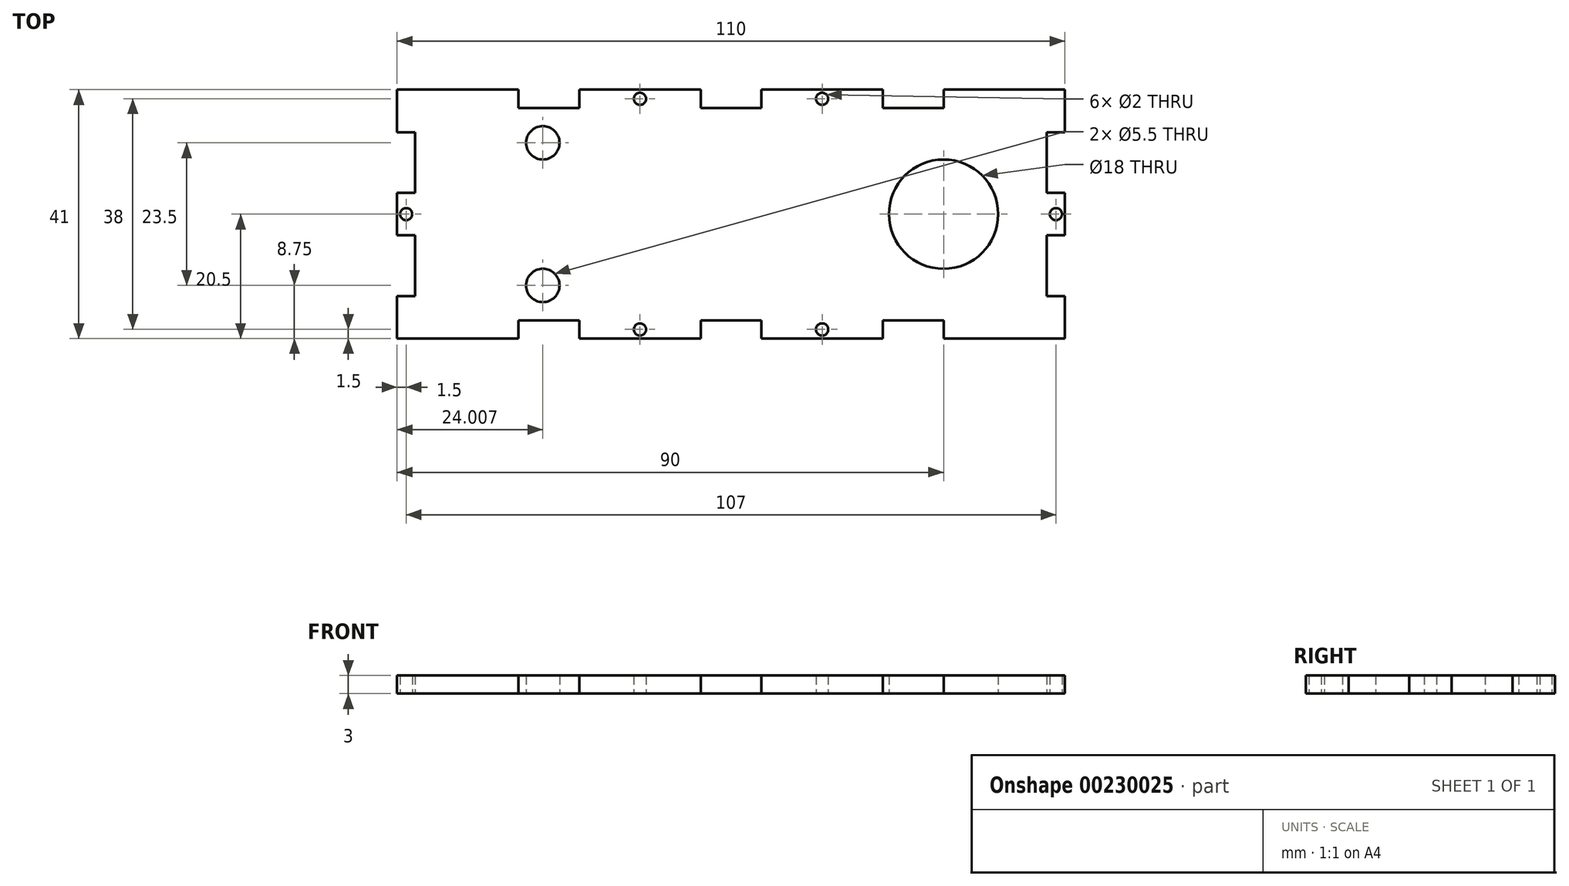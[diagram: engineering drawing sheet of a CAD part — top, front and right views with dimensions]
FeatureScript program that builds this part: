
annotation { "Feature Type Name" : "Feature", "Feature Type Description" : "" }
export const myFeature = defineFeature(function(context is Context, id is Id, definition is map)
    precondition{}
    {
        {
            var Q0;
            Q0=qCreatedBy(makeId("Top.planeOp"),FACE);
            var sketch = newSketch(context, id + "F0", { "sketchPlane" : qUnion([Q0])});
            skLineSegment(sketch, "E0", {"start": v(0, 0) * mm, "end": v(0, 7) * mm});
            skLineSegment(sketch, "E1", {"start": v(0, 7) * mm, "end": v(3, 7) * mm});
            skLineSegment(sketch, "E2", {"start": v(3, 7) * mm, "end": v(3, 17) * mm});
            skLineSegment(sketch, "E3", {"start": v(3, 17) * mm, "end": v(0, 17) * mm});
            skLineSegment(sketch, "E4", {"start": v(0, 17) * mm, "end": v(0, 24) * mm});
            skLineSegment(sketch, "E5", {"start": v(0, 24) * mm, "end": v(3, 24) * mm});
            skLineSegment(sketch, "E6", {"start": v(3, 24) * mm, "end": v(3, 34) * mm});
            skLineSegment(sketch, "E7", {"start": v(3, 34) * mm, "end": v(0, 34) * mm});
            skLineSegment(sketch, "E8", {"start": v(0, 34) * mm, "end": v(0, 41) * mm});
            skLineSegment(sketch, "E9", {"start": v(0, 41) * mm, "end": v(20, 41) * mm});
            skLineSegment(sketch, "E10", {"start": v(20, 41) * mm, "end": v(20, 38) * mm});
            skLineSegment(sketch, "E11", {"start": v(20, 38) * mm, "end": v(30, 38) * mm});
            skLineSegment(sketch, "E12", {"start": v(30, 38) * mm, "end": v(30, 41) * mm});
            skLineSegment(sketch, "E13", {"start": v(30, 41) * mm, "end": v(50, 41) * mm});
            skLineSegment(sketch, "E14", {"start": v(50, 38) * mm, "end": v(55, 38) * mm});
            skLineSegment(sketch, "E15", {"start": v(50, 41) * mm, "end": v(50, 38) * mm});
            skLineSegment(sketch, "E16", {"start": v(55, 40.92) * mm, "end": v(55, 0) * mm, "construction": true});
            skLineSegment(sketch, "E17", {"start": v(0, 20.5) * mm, "end": v(55, 20.5) * mm, "construction": true});
            skCircle(sketch, "E18", {"center": v(40, 39.5) * mm, "radius": 1 * mm});
            skPoint(sketch, "E18.centerSnap0", {"position": v(40, 41) * mm});
            skPoint(sketch, "E18.centerSnap1", {"position": v(50, 39.5) * mm});
            skCircle(sketch, "E19", {"center": v(1.5, 20.5) * mm, "radius": 1 * mm});
            skPoint(sketch, "E19.centerSnap0", {"position": v(1.5, 24) * mm});
            skLineSegment(sketch, "E20.MirrorCS", {"start": v(20, 0) * mm, "end": v(20, 3) * mm});
            skLineSegment(sketch, "E21.MirrorCS", {"start": v(50, 0) * mm, "end": v(50, 3) * mm});
            skLineSegment(sketch, "E22.MirrorCS", {"start": v(30, 3) * mm, "end": v(30, 0) * mm});
            skCircle(sketch, "E23.MirrorC", {"center": v(40, 1.5) * mm, "radius": 1 * mm});
            skLineSegment(sketch, "E24.MirrorCS", {"start": v(20, 3) * mm, "end": v(30, 3) * mm});
            skLineSegment(sketch, "E25.MirrorCS", {"start": v(30, 0) * mm, "end": v(50, 0) * mm});
            skPoint(sketch, "E26.MirrorP", {"position": v(40, 0) * mm});
            skPoint(sketch, "E27.MirrorP", {"position": v(50, 1.5) * mm});
            skLineSegment(sketch, "E28.MirrorCS", {"start": v(0, 0) * mm, "end": v(20, 0) * mm});
            skLineSegment(sketch, "E29.MirrorCS", {"start": v(50, 3) * mm, "end": v(55, 3) * mm});
            skLineSegment(sketch, "E30.MirrorCS", {"start": v(60, 41) * mm, "end": v(60, 38) * mm});
            skLineSegment(sketch, "E31.MirrorCS", {"start": v(107, 34) * mm, "end": v(110, 34) * mm});
            skLineSegment(sketch, "E32.MirrorCS", {"start": v(110, 24) * mm, "end": v(107, 24) * mm});
            skLineSegment(sketch, "E33.MirrorCS", {"start": v(110, 7) * mm, "end": v(107, 7) * mm});
            skLineSegment(sketch, "E34.MirrorCS", {"start": v(107, 17) * mm, "end": v(110, 17) * mm});
            skLineSegment(sketch, "E35.MirrorCS", {"start": v(90, 41) * mm, "end": v(90, 38) * mm});
            skLineSegment(sketch, "E36.MirrorCS", {"start": v(80, 38) * mm, "end": v(80, 41) * mm});
            skLineSegment(sketch, "E37.MirrorCS", {"start": v(60, 0) * mm, "end": v(60, 3) * mm});
            skCircle(sketch, "E38.MirrorC", {"center": v(108.5, 20.5) * mm, "radius": 1 * mm});
            skCircle(sketch, "E39.MirrorC", {"center": v(70, 1.5) * mm, "radius": 1 * mm});
            skCircle(sketch, "E40.MirrorC", {"center": v(70, 39.5) * mm, "radius": 1 * mm});
            skLineSegment(sketch, "E41.MirrorCS", {"start": v(110, 17) * mm, "end": v(110, 24) * mm});
            skLineSegment(sketch, "E42.MirrorCS", {"start": v(80, 41) * mm, "end": v(60, 41) * mm});
            skPoint(sketch, "E43.MirrorP", {"position": v(108.5, 24) * mm});
            skLineSegment(sketch, "E44.MirrorCS", {"start": v(90, 3) * mm, "end": v(80, 3) * mm});
            skLineSegment(sketch, "E45.MirrorCS", {"start": v(110, 0) * mm, "end": v(90, 0) * mm});
            skPoint(sketch, "E46.MirrorP", {"position": v(70, 41) * mm});
            skLineSegment(sketch, "E47.MirrorCS", {"start": v(107, 24) * mm, "end": v(107, 34) * mm});
            skPoint(sketch, "E48.MirrorP", {"position": v(60, 39.5) * mm});
            skLineSegment(sketch, "E49.MirrorCS", {"start": v(110, 0) * mm, "end": v(110, 7) * mm});
            skPoint(sketch, "E50.MirrorP", {"position": v(70, 0) * mm});
            skLineSegment(sketch, "E51.MirrorCS", {"start": v(110, 34) * mm, "end": v(110, 41) * mm});
            skLineSegment(sketch, "E52.MirrorCS", {"start": v(107, 7) * mm, "end": v(107, 17) * mm});
            skLineSegment(sketch, "E53.MirrorCS", {"start": v(110, 41) * mm, "end": v(90, 41) * mm});
            skLineSegment(sketch, "E54.MirrorCS", {"start": v(90, 38) * mm, "end": v(80, 38) * mm});
            skLineSegment(sketch, "E55.MirrorCS", {"start": v(80, 0) * mm, "end": v(60, 0) * mm});
            skLineSegment(sketch, "E56.MirrorCS", {"start": v(80, 3) * mm, "end": v(80, 0) * mm});
            skLineSegment(sketch, "E57.MirrorCS", {"start": v(90, 0) * mm, "end": v(90, 3) * mm});
            skPoint(sketch, "E58.MirrorP", {"position": v(60, 1.5) * mm});
            skLineSegment(sketch, "E59.MirrorCS", {"start": v(60, 3) * mm, "end": v(55, 3) * mm});
            skLineSegment(sketch, "E60.MirrorCS", {"start": v(60, 38) * mm, "end": v(55, 38) * mm});
            skCircle(sketch, "E61", {"center": v(90, 20.5) * mm, "radius": 9 * mm});
            skPoint(sketch, "E61.centerSnap0", {"position": v(110, 20.5) * mm});
            skPoint(sketch, "E62.centerSnap0", {"position": v(3, 29) * mm});
            skPoint(sketch, "E62.centerSnap1", {"position": v(25, 38) * mm});
            skPoint(sketch, "E63.centerSnap0", {"position": v(3, 12) * mm});
            skPoint(sketch, "E63.centerSnap1", {"position": v(25, 3) * mm});
            skCircle(sketch, "E64", {"center": v(24, 8.75) * mm, "radius": 2.75 * mm});
            skCircle(sketch, "E65.MirrorC", {"center": v(24, 32.25) * mm, "radius": 2.75 * mm});
            skSolve(sketch);
        }
        {
            var Q0;
            Q0 = qSketchRegion(id + "F0", true);
            extrude(context, id + "F1", {"entities" : qUnion([Q0]), "depth" : 3 * mm});
        }
    });
